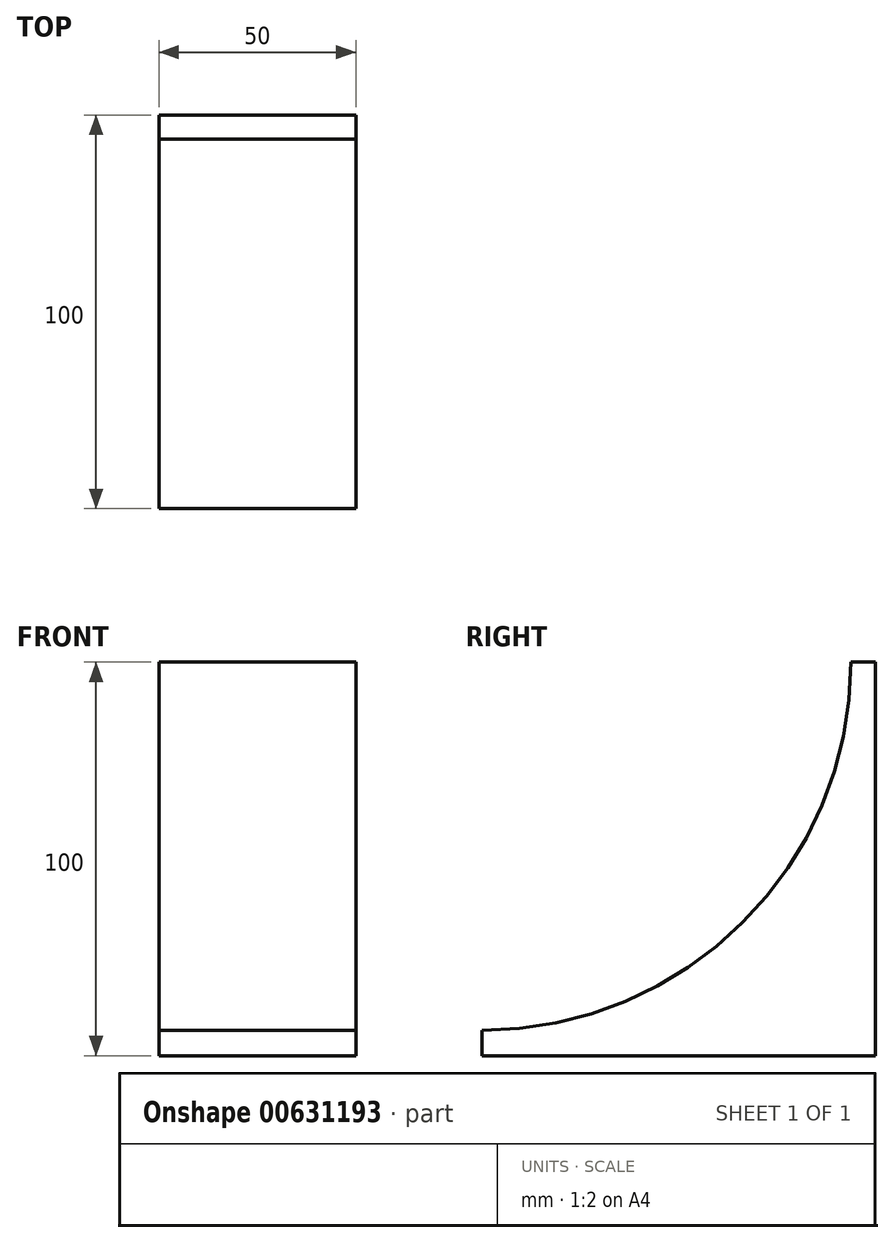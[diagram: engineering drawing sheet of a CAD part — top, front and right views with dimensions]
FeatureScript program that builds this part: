
annotation { "Feature Type Name" : "Feature", "Feature Type Description" : "" }
export const myFeature = defineFeature(function(context is Context, id is Id, definition is map)
    precondition{}
    {
        {
            var Q0;
            Q0=qCreatedBy(makeId("Right.planeOp"),FACE);
            var sketch = newSketch(context, id + "F0", { "sketchPlane" : qUnion([Q0])});
            skLineSegment(sketch, "E0.bottom", {"start": v(-22.8, 56.23) * mm, "end": v(77.2, 56.23) * mm});
            skLineSegment(sketch, "E0.top", {"start": v(-22.8, -43.77) * mm, "end": v(77.2, -43.77) * mm});
            skLineSegment(sketch, "E0.left", {"start": v(-22.8, 56.23) * mm, "end": v(-22.8, -43.77) * mm});
            skLineSegment(sketch, "E0.right", {"start": v(77.2, 56.23) * mm, "end": v(77.2, -43.77) * mm});
            skSolve(sketch);
        }
        {
            var Q0;
            Q0=makeQuery(id+"F0.imprint","IMPRINT",FACE,{"disambiguationData":[TD([[makeQuery(id+"F0.imprint","IMPRINT",EDGE,{"derivedFrom":sQuery(id+"F0.wireOp",EDGE,"E0.bottom")}),-1.0]])]});
            extrude(context, id + "F1", {"entities" : qUnion([Q0]), "depth" : 50 * mm, "offsetDistance" : 25 * mm});
        }
        {
            var Q0;
            Q0=qCreatedBy(makeId("Right.planeOp"),FACE);
            var sketch = newSketch(context, id + "F2", { "sketchPlane" : qUnion([Q0])});
            skCircle(sketch, "E1", {"center": v(-22.84, 56.51) * mm, "radius": 93.88 * mm});
            skSolve(sketch);
        }
        {
            var Q0;
            Q0=makeQuery(id+"F2.imprint","IMPRINT",FACE,{"disambiguationData":[TD([[makeQuery(id+"F2.imprint","IMPRINT",EDGE,{"derivedFrom":sQuery(id+"F2.wireOp",EDGE,"E1")}),1.0]])]});
            extrude(context, id + "F3", {"entities" : qUnion([Q0]), "depth" : 75 * mm, "offsetDistance" : 25 * mm});
        }
        {
            var Q0;
            Q0=makeQuery(id+"F3.opExtrude","SWEPT_BODY",BODY,{"disambiguationData":[OSD([sQuery(id+"F2.wireOp",EDGE,"E1")])]});
            var Q1;
            Q1=makeQuery(id+"F1.opExtrude","SWEPT_BODY",BODY,{"disambiguationData":[OSD([sQuery(id+"F0.wireOp",EDGE,"E0.bottom"),sQuery(id+"F0.wireOp",EDGE,"E0.top"),sQuery(id+"F0.wireOp",EDGE,"E0.left"),sQuery(id+"F0.wireOp",EDGE,"E0.right")])]});
            booleanBodies(context, id + "F4", {"operationType" : BooleanOperationType.SUBTRACTION, "tools" : qUnion([Q0]), "targets" : qUnion([Q1])});
        }
    });
